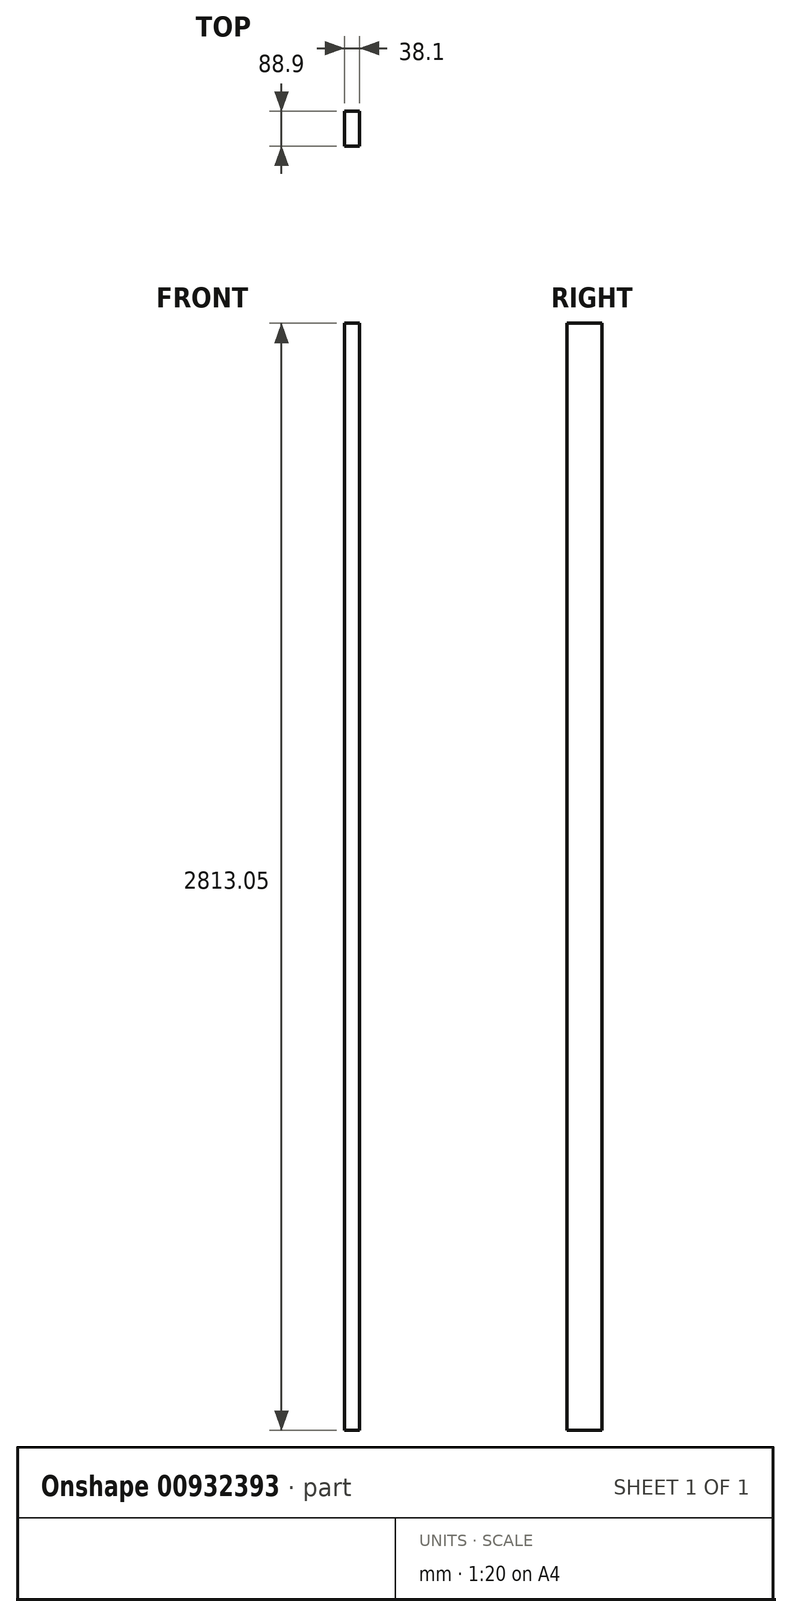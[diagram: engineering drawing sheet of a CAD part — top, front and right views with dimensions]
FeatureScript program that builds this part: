
annotation { "Feature Type Name" : "Feature", "Feature Type Description" : "" }
export const myFeature = defineFeature(function(context is Context, id is Id, definition is map)
    precondition{}
    {
        {
            var Q0;
            Q0=qCreatedBy(makeId("Top.planeOp"),FACE);
            var sketch = newSketch(context, id + "F0", { "sketchPlane" : qUnion([Q0])});
            skLineSegment(sketch, "E0.bottom", {"start": v(19.05, 44.45) * mm, "end": v(-19.05, 44.45) * mm});
            skLineSegment(sketch, "E0.top", {"start": v(19.05, -44.45) * mm, "end": v(-19.05, -44.45) * mm});
            skLineSegment(sketch, "E0.left", {"start": v(19.05, 44.45) * mm, "end": v(19.05, -44.45) * mm});
            skLineSegment(sketch, "E0.right", {"start": v(-19.05, 44.45) * mm, "end": v(-19.05, -44.45) * mm});
            skPoint(sketch, "E0.middle", {"position": v(0, 0) * mm});
            skSolve(sketch);
        }
        {
            var Q0;
            Q0=makeQuery(id+"F0.imprint","IMPRINT",FACE,{"disambiguationData":[TD([[makeQuery(id+"F0.imprint","IMPRINT",EDGE,{"derivedFrom":sQuery(id+"F0.wireOp",EDGE,"E0.bottom")}),1.0]])]});
            extrude(context, id + "F1", {"entities" : qUnion([Q0]), "depth" : 2813.05 * mm, "offsetDistance" : 25.4 * mm});
        }
    });
